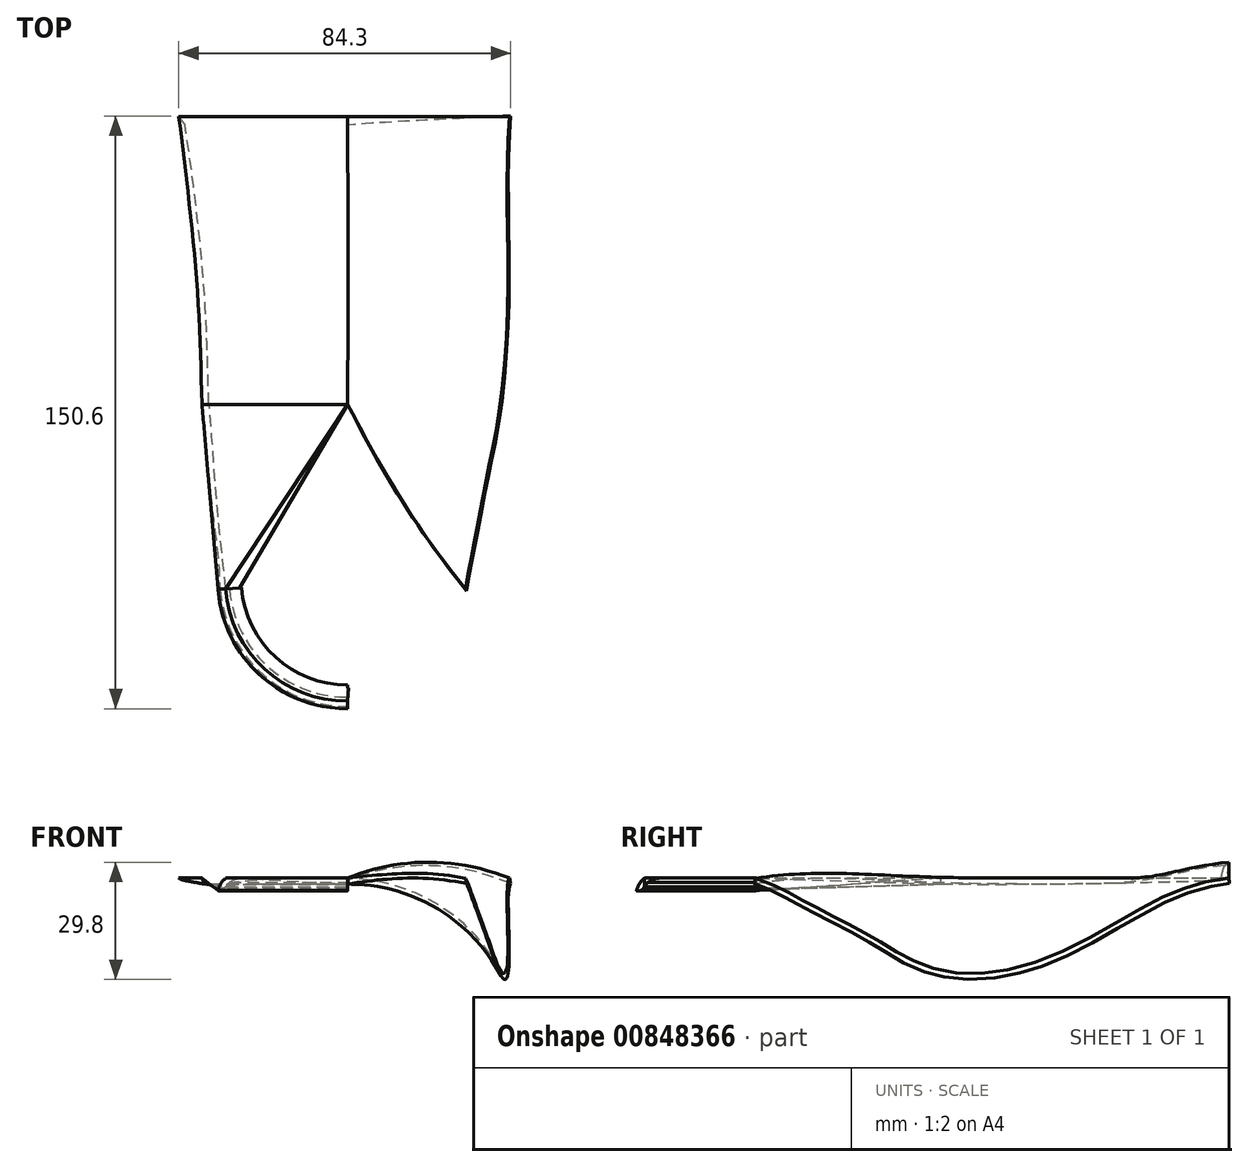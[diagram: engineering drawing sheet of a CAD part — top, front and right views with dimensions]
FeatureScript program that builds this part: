
annotation { "Feature Type Name" : "Feature", "Feature Type Description" : "" }
export const myFeature = defineFeature(function(context is Context, id is Id, definition is map)
    precondition{}
    {
        {
            var Q0;
            Q0=qCreatedBy(makeId("Top.planeOp"),FACE);
            var sketch = newSketch(context, id + "F0", { "sketchPlane" : qUnion([Q0])});
            skLineSegment(sketch, "E0", {"start": v(0.1, -101.9) * mm, "end": v(0.1, 73.1) * mm, "construction": true});
            skLineSegment(sketch, "E1", {"start": v(-33.53, -0.16) * mm, "end": v(36.47, -0.16) * mm, "construction": true});
            skArc(sketch, "E2", {"start": v(-29.9, -46.9) * mm, "mid": v(0.1, -76.9) * mm, "end": v(30.1, -46.9) * mm});
            skLineSegment(sketch, "E3", {"start": v(-29.9, -46.9) * mm, "end": v(30.1, -46.9) * mm});
            skLineSegment(sketch, "E4", {"start": v(41.11, 24.42) * mm, "end": v(-33.89, 24.42) * mm, "construction": true});
            skSolve(sketch);
        }
        {
            var Q0;
            Q0=qCreatedBy(makeId("Top.planeOp"),FACE);
            var sketch = newSketch(context, id + "F1", { "sketchPlane" : qUnion([Q0])});
            skLineSegment(sketch, "E5", {"start": v(30, -46.9) * mm, "end": v(0, -46.9) * mm});
            skLineSegment(sketch, "E6", {"start": v(0, -46.9) * mm, "end": v(-32.5, -46.9) * mm});
            skLineSegment(sketch, "E7", {"start": v(0, -46.9) * mm, "end": v(0, -76.9) * mm});
            skArc(sketch, "E8", {"start": v(0, -76.9) * mm, "mid": v(21.21, -68.12) * mm, "end": v(30, -46.9) * mm});
            skArc(sketch, "E9", {"start": v(-32.5, -46.9) * mm, "mid": v(-22.14, -68.29) * mm, "end": v(0, -76.9) * mm});
            skLineSegment(sketch, "E10", {"start": v(0, -46.9) * mm, "end": v(0, -0.25) * mm});
            skLineSegment(sketch, "E11", {"start": v(0, -0.25) * mm, "end": v(36, -0.25) * mm});
            skLineSegment(sketch, "E12", {"start": v(0, -0.25) * mm, "end": v(-37, -0.25) * mm});
            skLineSegment(sketch, "E13", {"start": v(0, -0.25) * mm, "end": v(0.14, 24.4) * mm});
            skLineSegment(sketch, "E14", {"start": v(0.14, 24.4) * mm, "end": v(-37.86, 24.4) * mm});
            skLineSegment(sketch, "E15", {"start": v(0.14, 24.4) * mm, "end": v(41.14, 24.4) * mm});
            skLineSegment(sketch, "E16", {"start": v(0.14, 24.4) * mm, "end": v(0.14, 73.1) * mm});
            skLineSegment(sketch, "E17", {"start": v(0.14, 73.1) * mm, "end": v(-42.86, 73.1) * mm});
            skLineSegment(sketch, "E18", {"start": v(0.14, 73.1) * mm, "end": v(41.14, 72.87) * mm});
            skFitSpline(sketch, "E19", {"points": [v(-32.5, -46.9) * mm, v(-37, -0.25) * mm, v(-37.86, 24.4) * mm, v(-42.86, 73.1) * mm], "startDerivative": vector(-22.4, 132.76) * mm, "endDerivative": vector(9.8, 158.53) * mm});
            skArc(sketch, "E20.0", {"start": v(0, -75.4) * mm, "mid": v(20.15, -67.06) * mm, "end": v(28.5, -46.9) * mm});
            skArc(sketch, "E20.1", {"start": v(-31, -46.9) * mm, "mid": v(-21.08, -67.23) * mm, "end": v(0, -75.4) * mm});
            skSolve(sketch);
        }
        {
            var Q0;
            Q0=qCreatedBy(makeId("Right.planeOp"),FACE);
            var sketch = newSketch(context, id + "F2", { "sketchPlane" : qUnion([Q0])});
            skFitSpline(sketch, "E21", {"points": [v(73.17, -0.38) * mm, v(50.67, -3.03) * mm, v(23.41, -7.47) * mm, v(-1.62, -9.68) * mm, v(-19.22, -7.72) * mm, v(-35.85, -4.61) * mm, v(-48.65, -2.2) * mm, v(-72.33, -0.06) * mm], "startDerivative": vector(-144.4, -14.69) * mm, "endDerivative": vector(-116.57, 5.31) * mm});
            skFitSpline(sketch, "E22", {"points": [v(-72.33, -0.06) * mm, v(-72.25, -0.06) * mm, v(-83.36, -1.5) * mm, v(-95.14, -4.97) * mm, v(-101.83, -10.1) * mm], "startDerivative": vector(-32.67, 0.6) * mm, "endDerivative": vector(-25.97, -24.15) * mm});
            skSolve(sketch);
        }
        {
            var Q0;
            Q0=qCreatedBy(makeId("Front.planeOp"),FACE);
            var sketch = newSketch(context, id + "F3", { "sketchPlane" : qUnion([Q0])});
            skPoint(sketch, "E23.0", {"position": v(0, 0) * mm});
            skArc(sketch, "E24", {"start": v(36.02, -22) * mm, "mid": v(21.14, -5.88) * mm, "end": v(0, 0) * mm});
            skArc(sketch, "E25.0", {"start": v(34.69, -22.68) * mm, "mid": v(20.36, -7.16) * mm, "end": v(0, -1.5) * mm});
            skLineSegment(sketch, "E26", {"start": v(34.69, -22.68) * mm, "end": v(36.02, -22) * mm});
            skLineSegment(sketch, "E27", {"start": v(0, -1.5) * mm, "end": v(0, 0) * mm});
            skPoint(sketch, "E28.0", {"position": v(-37, 0) * mm});
            skLineSegment(sketch, "E29.bottom", {"start": v(-37, 0) * mm, "end": v(0, 0) * mm});
            skLineSegment(sketch, "E29.top", {"start": v(-37, -1.5) * mm, "end": v(0, -1.5) * mm});
            skLineSegment(sketch, "E29.left", {"start": v(-37, 0) * mm, "end": v(-37, -1.5) * mm});
            skLineSegment(sketch, "E29.right", {"start": v(0, 0) * mm, "end": v(0, -1.5) * mm});
            skPoint(sketch, "E30.0", {"position": v(36, 0) * mm});
            skLineSegment(sketch, "E31", {"start": v(36, 0) * mm, "end": v(36.02, -22) * mm, "construction": true});
            skSolve(sketch);
        }
        {
            var Q0;
            Q0=sQuery(id+"F0.wireOp",EDGE,"E4");
            cPlane(context, id + "F4", {"entities" : qUnion([Q0]), "cplaneType" : CPlaneType.LINE_ANGLE, "offset" : 25 * mm, "angle" : 0 * degree, "width" : 150 * mm, "height" : 150 * mm});
        }
        {
            var Q0;
            Q0=qCreatedBy(id+"F4.planeOp",FACE);
            var sketch = newSketch(context, id + "F5", { "sketchPlane" : qUnion([Q0])});
            skPoint(sketch, "E32.0", {"position": v(41.14, 0) * mm});
            skLineSegment(sketch, "E33", {"start": v(41.14, 0) * mm, "end": v(42.22, -22) * mm, "construction": true});
            skPoint(sketch, "E34.0", {"position": v(0.14, 0) * mm});
            skArc(sketch, "E35", {"start": v(42.22, -22) * mm, "mid": v(24.16, -5.3) * mm, "end": v(0.14, 0) * mm});
            skArc(sketch, "E36.0", {"start": v(40.95, -22.8) * mm, "mid": v(23.47, -6.62) * mm, "end": v(0.2, -1.5) * mm});
            skLineSegment(sketch, "E37", {"start": v(42.22, -22) * mm, "end": v(40.95, -22.8) * mm});
            skLineSegment(sketch, "E38", {"start": v(0.2, -1.5) * mm, "end": v(0.14, 0) * mm});
            skPoint(sketch, "E39.0", {"position": v(-37.86, 0) * mm});
            skLineSegment(sketch, "E40.bottom", {"start": v(-37.86, 0) * mm, "end": v(0.2, 0) * mm});
            skLineSegment(sketch, "E40.top", {"start": v(-37.86, -1.5) * mm, "end": v(0.2, -1.5) * mm});
            skLineSegment(sketch, "E40.left", {"start": v(-37.86, 0) * mm, "end": v(-37.86, -1.5) * mm});
            skLineSegment(sketch, "E40.right", {"start": v(0.2, 0) * mm, "end": v(0.2, -1.5) * mm});
            skSolve(sketch);
        }
        {
            var Q0;
            Q0=sQuery(id+"F0.wireOp",EDGE,"E2");
            cPoint(context, id + "F6", {"entities" : qUnion([Q0]), "parameter" : 0.5});
        }
        {
            var Q0;
            Q0=qCreatedBy(id+"F6",VERTEX);
            var Q1;
            Q1=sQuery(id+"F0.wireOp",EDGE,"E0");
            cPlane(context, id + "F7", {"entities" : qUnion([Q0, Q1]), "cplaneType" : CPlaneType.CURVE_POINT, "offset" : 25 * mm, "width" : 150 * mm, "height" : 150 * mm});
        }
        {
            var Q0;
            Q0=sQuery(id+"F2.wireOp",VERTEX,"E21.start");
            var Q1;
            Q1=sQuery(id+"F2.wireOp",EDGE,"E21");
            cPlane(context, id + "F8", {"entities" : qUnion([Q0, Q1]), "cplaneType" : CPlaneType.CURVE_POINT, "offset" : 25 * mm, "width" : 150 * mm, "height" : 150 * mm});
        }
        {
            var Q0;
            Q0=qCreatedBy(id+"F8.planeOp",FACE);
            var sketch = newSketch(context, id + "F9", { "sketchPlane" : qUnion([Q0])});
            skPoint(sketch, "E41.0", {"position": v(0, -7.78) * mm});
            skPoint(sketch, "E42.0", {"position": v(-42.86, -7.4) * mm});
            skLineSegment(sketch, "E43.bottom", {"start": v(-42.86, -7.4) * mm, "end": v(0, -7.4) * mm});
            skLineSegment(sketch, "E43.top", {"start": v(-42.86, -7.9) * mm, "end": v(0, -7.9) * mm});
            skLineSegment(sketch, "E43.left", {"start": v(-42.86, -7.4) * mm, "end": v(-42.86, -7.9) * mm});
            skLineSegment(sketch, "E43.right", {"start": v(0, -7.4) * mm, "end": v(0, -7.9) * mm});
            skLineSegment(sketch, "E44.bottom", {"start": v(0, -7.9) * mm, "end": v(40.82, -7.9) * mm});
            skLineSegment(sketch, "E44.top", {"start": v(0, -7.4) * mm, "end": v(40.82, -7.4) * mm});
            skLineSegment(sketch, "E44.left", {"start": v(0, -7.9) * mm, "end": v(0, -7.4) * mm});
            skLineSegment(sketch, "E44.right", {"start": v(40.82, -7.9) * mm, "end": v(40.82, -7.4) * mm});
            skSolve(sketch);
        }
        {
            var Q0;
            Q0=qCreatedBy(makeId("Right.planeOp"),FACE);
            var sketch = newSketch(context, id + "F10", { "sketchPlane" : qUnion([Q0])});
            skLineSegment(sketch, "E45.MirrorCS", {"start": v(-75.83, -3.15) * mm, "end": v(-77.4, -3.32) * mm});
            skLineSegment(sketch, "E46.MirrorCS", {"start": v(-71.33, 0) * mm, "end": v(-75.4, 0) * mm});
            skArc(sketch, "E47.MirrorCS", {"start": v(-77.4, -3.32) * mm, "mid": v(-76.66, -1.5) * mm, "end": v(-75.4, 0) * mm});
            skArc(sketch, "E48.MirrorCS", {"start": v(-75.83, -3.15) * mm, "mid": v(-74.08, -0.87) * mm, "end": v(-71.33, 0) * mm});
            skSolve(sketch);
        }
        {
            var Q0;
            Q0=sQuery(id+"F1.wireOp",EDGE,"E6");
            cPlane(context, id + "F11", {"entities" : qUnion([Q0]), "cplaneType" : CPlaneType.LINE_ANGLE, "offset" : 25 * mm, "angle" : 0 * degree, "width" : 150 * mm, "height" : 150 * mm});
        }
        {
            var Q0;
            Q0=qCreatedBy(id+"F11.planeOp",FACE);
            var sketch = newSketch(context, id + "F12", { "sketchPlane" : qUnion([Q0])});
            skLineSegment(sketch, "E49.MirrorCS", {"start": v(-27.6, 0) * mm, "end": v(-31, 0) * mm});
            skLineSegment(sketch, "E50.MirrorCS", {"start": v(-31.35, -3.1) * mm, "end": v(-32.92, -3.1) * mm});
            skArc(sketch, "E51.MirrorCS", {"start": v(-32.92, -3.1) * mm, "mid": v(-32.19, -1.4) * mm, "end": v(-31, 0) * mm});
            skArc(sketch, "E52.MirrorCS", {"start": v(-31.35, -3.1) * mm, "mid": v(-29.9, -1.03) * mm, "end": v(-27.6, 0) * mm});
            skPoint(sketch, "E53.0", {"position": v(-31, 0) * mm});
            skSolve(sketch);
        }
        {
            var Q0;
            Q0=makeQuery(id+"F12.imprint","IMPRINT",FACE,{"disambiguationData":[TD([[makeQuery(id+"F12.imprint","IMPRINT",EDGE,{"derivedFrom":sQuery(id+"F12.wireOp",EDGE,"E49.MirrorCS")}),1.0]])]});
            var Q1;
            Q1=makeQuery(id+"F3.imprint","IMPRINT",FACE,{"disambiguationData":[TD([[makeQuery(id+"F3.imprint","IMPRINT",EDGE,{"derivedFrom":sQuery(id+"F3.wireOp",EDGE,"E29.bottom")}),-1.0]])]});
            loft(context, id + "F13", {"sheetProfilesArray" : [{ "sheetProfileEntities" : qUnion([Q0]) }, { "sheetProfileEntities" : qUnion([Q1]) }]});
        }
        {
            var Q0;
            Q0=makeQuery(id+"F13.opLoft","SWEPT_EDGE",EDGE,{"disambiguationData":[OSD([sQuery(id+"F3.wireOp",EDGE,"E29.top"),sQuery(id+"F3.wireOp",EDGE,"E29.left"),sQuery(id+"F12.wireOp",EDGE,"E50.MirrorCS"),sQuery(id+"F12.wireOp",EDGE,"E52.MirrorCS")])]});
            fillet(context, id + "F14", {"entities" : qUnion([Q0]), "radius" : 1.85 * mm, "tangentPropagation" : true, "allowEdgeOverflow" : false});
        }
        {
            var Q0;
            Q0=makeQuery(id+"F10.imprint","IMPRINT",FACE,{"disambiguationData":[TD([[makeQuery(id+"F10.imprint","IMPRINT",EDGE,{"derivedFrom":sQuery(id+"F10.wireOp",EDGE,"E45.MirrorCS")}),-1.0]])]});
            var Q1;
            Q1=makeQuery(id+"F13.opLoft","CAP_FACE",FACE,{"disambiguationData":[OSD([makeQuery(id+"F12.imprint","IMPRINT",FACE,{"disambiguationData":[TD([[makeQuery(id+"F12.imprint","IMPRINT",EDGE,{"derivedFrom":sQuery(id+"F12.wireOp",EDGE,"E49.MirrorCS")}),1.0]])]})])],"isStart":true});
            var Q2;
            Q2=sQuery(id+"F1.wireOp",EDGE,"E20.1");
            sweep(context, id + "F15", {"operationType" : NewBodyOperationType.ADD, "profiles" : qUnion([Q0, Q1]), "path" : qUnion([Q2])});
        }
        {
            var Q0;
            Q0=makeQuery(id+"F15.opSweep","SWEPT_EDGE",EDGE,{"disambiguationData":[OSD([sQuery(id+"F1.wireOp",EDGE,"E20.1"),sQuery(id+"F10.wireOp",EDGE,"E45.MirrorCS"),sQuery(id+"F10.wireOp",EDGE,"E48.MirrorCS")])]});
            fillet(context, id + "F16", {"entities" : qUnion([Q0]), "radius" : 1.68 * mm, "tangentPropagation" : true, "allowEdgeOverflow" : false});
        }
        {
            var Q0;
            Q0=makeQuery(id+"F15.opSweep","SWEPT_EDGE",EDGE,{"disambiguationData":[OSD([sQuery(id+"F1.wireOp",EDGE,"E20.1"),sQuery(id+"F10.wireOp",EDGE,"E45.MirrorCS"),sQuery(id+"F10.wireOp",EDGE,"E47.MirrorCS")])]});
            fillet(context, id + "F17", {"entities" : qUnion([Q0]), "radius" : 0.14 * mm, "tangentPropagation" : true, "allowEdgeOverflow" : false});
        }
        {
            var Q1;
            Q1=makeQuery(id+"F3.imprint","IMPRINT",FACE,{"disambiguationData":[TD([[makeQuery(id+"F3.imprint","IMPRINT",EDGE,{"derivedFrom":sQuery(id+"F3.wireOp",EDGE,"E29.bottom")}),-1.0]])]});
            var Q2;
            {var subQ0=sQuery(id+"F5.wireOp",EDGE,"E38");Q2=makeQuery(id+"F5.imprint","IMPRINT",FACE,{"disambiguationData":[TD([[makeQuery(id+"F5.imprint","IMPRINT",EDGE,{"derivedFrom":subQ0}),1.0]])]});}
            var Q3;
            Q3=makeQuery(id+"F9.imprint","IMPRINT",FACE,{"disambiguationData":[TD([[makeQuery(id+"F9.imprint","IMPRINT",EDGE,{"derivedFrom":sQuery(id+"F9.wireOp",EDGE,"E43.bottom")}),-1.0]])]});
            loft(context, id + "F18", {"operationType" : NewBodyOperationType.ADD, "sheetProfilesArray" : [{ "sheetProfileEntities" : qUnion([Q1]) }, { "sheetProfileEntities" : qUnion([Q2]) }, { "sheetProfileEntities" : qUnion([Q3]) }]});
        }
        {
            var Q0;
            Q0=makeQuery(id+"F18.opLoft","SWEPT_EDGE",EDGE,{"disambiguationData":[OSD([sQuery(id+"F3.wireOp",EDGE,"E29.top"),sQuery(id+"F3.wireOp",EDGE,"E29.left"),sQuery(id+"F5.wireOp",EDGE,"E40.top"),sQuery(id+"F5.wireOp",EDGE,"E40.left"),sQuery(id+"F9.wireOp",EDGE,"E43.top"),sQuery(id+"F9.wireOp",EDGE,"E43.left")])]});
            fillet(context, id + "F19", {"entities" : qUnion([Q0]), "radius" : 1.76 * mm, "tangentPropagation" : true, "allowEdgeOverflow" : false});
        }
        {
            var Q0;
            Q0=makeQuery(id+"F18.opLoft","MID_CAP_EDGE",EDGE,{"disambiguationData":[OSD([sQuery(id+"F9.wireOp",EDGE,"E43.top"),sQuery(id+"F9.wireOp",EDGE,"E43.left"),sQuery(id+"F9.wireOp",EDGE,"E43.right")])],"capPos":2.0});
            var Q1;
            {var subQ0=sQuery(id+"F9.wireOp",EDGE,"E43.top");var subQ1=sQuery(id+"F9.wireOp",EDGE,"E43.left");Q1=makeQuery(id+"F19.opFillet","BLEND_EDGE",EDGE,{"blendedFrom":[makeQuery(id+"F18.opLoft","SWEPT_EDGE",EDGE,{"disambiguationData":[OSD([sQuery(id+"F3.wireOp",EDGE,"E29.top"),sQuery(id+"F3.wireOp",EDGE,"E29.left"),sQuery(id+"F5.wireOp",EDGE,"E40.top"),sQuery(id+"F5.wireOp",EDGE,"E40.left"),subQ0,subQ1])]}),makeQuery(id+"F18.opLoft","CAP_FACE",FACE,{"disambiguationData":[OSD([makeQuery(id+"F9.imprint","IMPRINT",FACE,{"disambiguationData":[TD([[makeQuery(id+"F9.imprint","IMPRINT",EDGE,{"derivedFrom":sQuery(id+"F9.wireOp",EDGE,"E43.bottom")}),-1.0]])]})])],"isStart":true})],"blendedInto":[makeQuery(id+"F18.opLoft","CAP_FACE",FACE,{"disambiguationData":[OSD([makeQuery(id+"F9.imprint","IMPRINT",FACE,{"disambiguationData":[TD([[makeQuery(id+"F9.imprint","IMPRINT",EDGE,{"derivedFrom":sQuery(id+"F9.wireOp",EDGE,"E43.bottom")}),-1.0]])]})])],"isStart":true})]});}
            fillet(context, id + "F20", {"entities" : qUnion([Q0, Q1]), "radius" : 5 * mm, "tangentPropagation" : true, "allowEdgeOverflow" : false});
        }
        {
            var Q0;
            Q0=qCreatedBy(makeId("Top.planeOp"),FACE);
            var sketch = newSketch(context, id + "F21", { "sketchPlane" : qUnion([Q0])});
            skLineSegment(sketch, "E54", {"start": v(30.01, -46.98) * mm, "end": v(41.15, 72.82) * mm, "construction": true});
            skSolve(sketch);
        }
        {
            var Q0;
            Q0 = qBodyType(qCreatedBy(id + "F21" ,EDGE), BodyType.WIRE);
            cPlane(context, id + "F22", {"entities" : qUnion([Q0]), "cplaneType" : CPlaneType.LINE_ANGLE, "offset" : 25 * mm, "angle" : 120 * degree, "width" : 150 * mm, "height" : 150 * mm});
        }
        {
            var Q0;
            Q0=sQuery(id+"F1.wireOp",VERTEX,"E5.start");
            var Q1;
            Q1=sQuery(id+"F1.wireOp",VERTEX,"E18.end");
            var Q2;
            Q2=sQuery(id+"F5.wireOp",VERTEX,"E36.0.start");
            var Q3;
            Q3 = qBodyType(qCreatedBy(id + "F24" ,EDGE), BodyType.WIRE);
            cPlane(context, id + "F23", {"entities" : qUnion([Q0, Q1, Q2, Q3]), "cplaneType" : CPlaneType.THREE_POINT, "offset" : 25 * mm, "width" : 150 * mm, "height" : 150 * mm});
        }
        {
            var Q0;
            Q0=qCreatedBy(id+"F23.planeOp",FACE);
            var sketch = newSketch(context, id + "F24", { "sketchPlane" : qUnion([Q0])});
            skFitSpline(sketch, "E55", {"points": [v(76.48, -7.6) * mm, v(56.81, -13.7) * mm, v(27.4, -28.5) * mm, v(2, -29.96) * mm, v(-12.12, -22.86) * mm, v(-23.25, -16.41) * mm, v(-33.58, -10.77) * mm, v(-44.1, -5.58) * mm], "startDerivative": vector(-144.4, -14.69) * mm, "endDerivative": vector(-118.49, 43.27) * mm});
            skFitSpline(sketch, "E56.0", {"points": [v(76.63, -9.08) * mm, v(75.16, -9.23) * mm, v(72.38, -9.62) * mm, v(68.52, -10.5) * mm, v(64.8, -11.7) * mm, v(61.03, -13.26) * mm, v(57.07, -15.2) * mm, v(52.78, -17.56) * mm, v(48.2, -20.16) * mm, v(43.42, -22.85) * mm, v(38.45, -25.48) * mm, v(33.36, -27.88) * mm, v(29.05, -29.58) * mm, v(25.58, -30.66) * mm, v(22.12, -31.55) * mm, v(17.84, -32.33) * mm, v(12.85, -32.73) * mm, v(8.08, -32.61) * mm, v(4.34, -32.08) * mm, v(1.53, -31.41) * mm, v(-1.14, -30.57) * mm, v(-4.22, -29.27) * mm, v(-7.58, -27.46) * mm, v(-10.17, -25.86) * mm, v(-12.15, -24.61) * mm, v(-14.09, -23.4) * mm, v(-16.48, -21.96) * mm, v(-19.34, -20.3) * mm, v(-22.19, -18.7) * mm, v(-25.05, -17.14) * mm, v(-27.94, -15.58) * mm, v(-30.3, -14.3) * mm, v(-32.14, -13.3) * mm, v(-33.5, -12.54) * mm, v(-34.8, -11.8) * mm, v(-36.08, -11.07) * mm, v(-37.33, -10.36) * mm, v(-39.02, -9.44) * mm, v(-41.28, -8.31) * mm, v(-43.42, -7.43) * mm, v(-44.62, -7) * mm]});
            skLineSegment(sketch, "E57", {"start": v(-44.62, -7) * mm, "end": v(-44.1, -5.58) * mm});
            skLineSegment(sketch, "E58", {"start": v(76.63, -9.08) * mm, "end": v(76.48, -7.6) * mm});
            skSolve(sketch);
        }
        {
            var Q0;
            Q0=sQuery(id+"F5.wireOp",EDGE,"E36.0");
            var Q2;
            Q2=makeQuery(id+"F24.imprint","IMPRINT",FACE,{"disambiguationData":[TD([[makeQuery(id+"F24.imprint","IMPRINT",EDGE,{"derivedFrom":sQuery(id+"F24.wireOp",EDGE,"E55")}),1.0]])]});
            var Q3;
            Q3=makeQuery(id+"F18.opLoft","SWEPT_FACE",FACE,{"disambiguationData":[OSD([sQuery(id+"F3.wireOp",EDGE,"E24"),sQuery(id+"F3.wireOp",EDGE,"E25.0"),sQuery(id+"F3.wireOp",EDGE,"E29.bottom"),sQuery(id+"F3.wireOp",EDGE,"E29.top"),sQuery(id+"F3.wireOp",EDGE,"E29.right"),sQuery(id+"F5.wireOp",EDGE,"E35"),sQuery(id+"F5.wireOp",EDGE,"E36.0"),sQuery(id+"F5.wireOp",EDGE,"E38"),sQuery(id+"F5.wireOp",EDGE,"E40.bottom"),sQuery(id+"F5.wireOp",EDGE,"E40.top"),sQuery(id+"F5.wireOp",EDGE,"E40.right"),sQuery(id+"F9.wireOp",EDGE,"E43.bottom"),sQuery(id+"F9.wireOp",EDGE,"E43.top"),sQuery(id+"F9.wireOp",EDGE,"E44.bottom"),sQuery(id+"F9.wireOp",EDGE,"E44.top"),sQuery(id+"F9.wireOp",EDGE,"E44.left")])]});
            loft(context, id + "F25", {"operationType" : NewBodyOperationType.ADD, "addSections" : true, "spine" : qUnion([Q0]), "sectionCount" : 5, "sheetProfilesArray" : [{ "sheetProfileEntities" : qUnion([Q2]) }, { "sheetProfileEntities" : qUnion([Q3]) }]});
        }
    });
